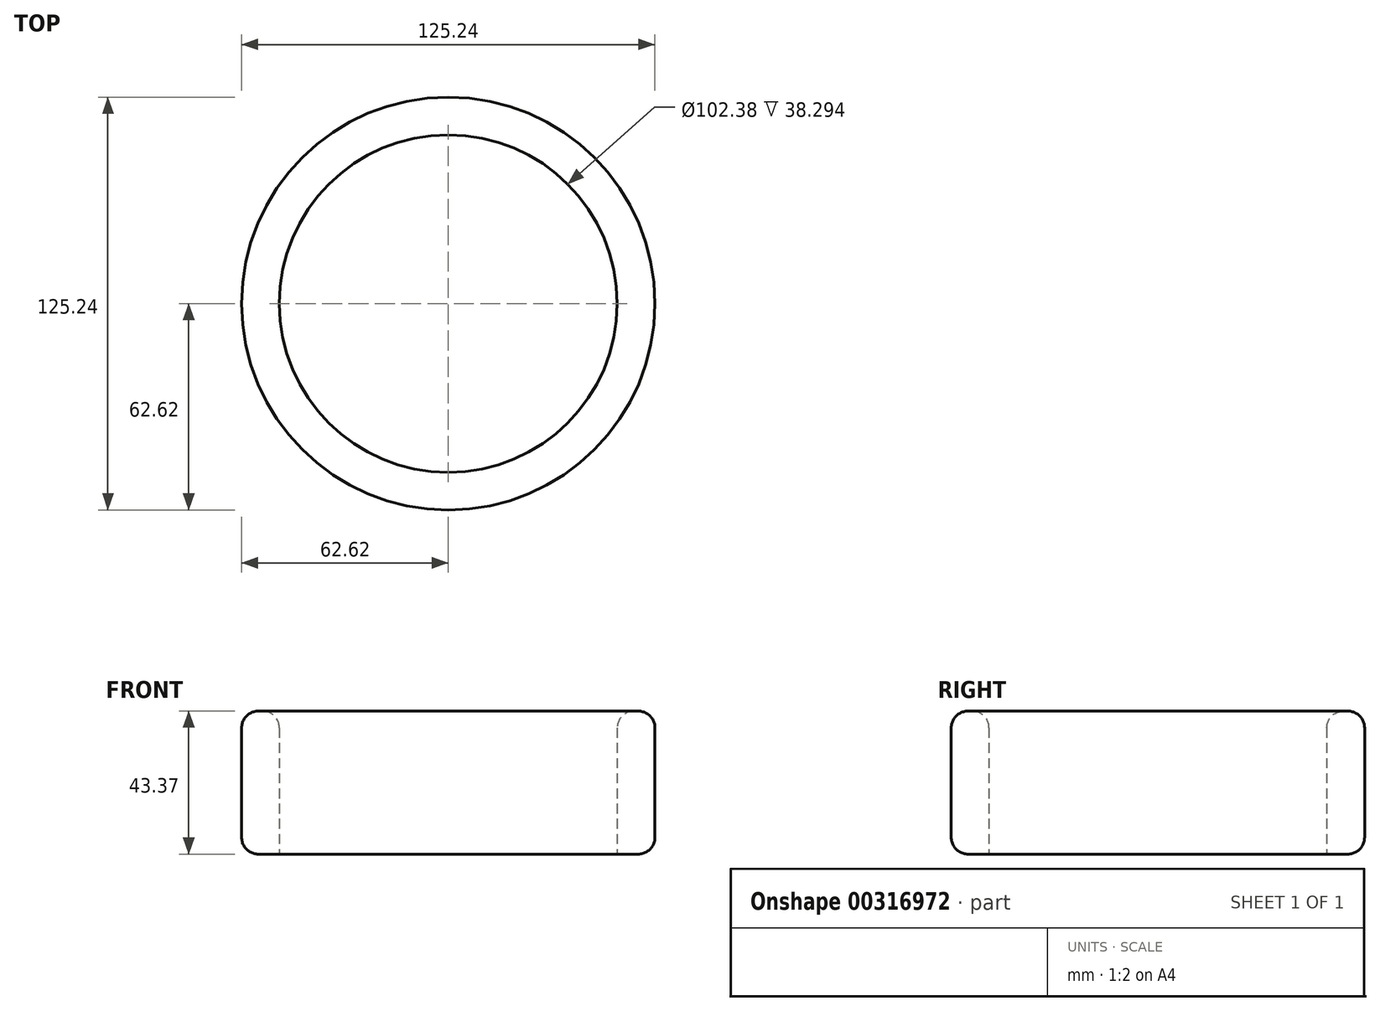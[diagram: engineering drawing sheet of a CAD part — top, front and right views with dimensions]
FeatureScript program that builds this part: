
annotation { "Feature Type Name" : "Feature", "Feature Type Description" : "" }
export const myFeature = defineFeature(function(context is Context, id is Id, definition is map)
    precondition{}
    {
        {
            var Q0;
            Q0=qCreatedBy(makeId("Top.planeOp"),FACE);
            var sketch = newSketch(context, id + "F0", { "sketchPlane" : qUnion([Q0])});
            skCircle(sketch, "E0", {"center": v(0, 0) * mm, "radius": 62.62 * mm});
            skSolve(sketch);
        }
        {
            var Q0;
            Q0 = qSketchRegion(id + "F0", true);
            extrude(context, id + "F1", {"entities" : qUnion([Q0]), "depth" : 43.37 * mm});
        }
        {
            var Q0;
            Q0=makeQuery(id+"F1.opExtrude","CAP_FACE",FACE,{"disambiguationData":[OSD([sQuery(id+"F0.wireOp",EDGE,"E0")])],"isStart":true});
            var sketch = newSketch(context, id + "F2", { "sketchPlane" : qUnion([Q0])});
            skCircle(sketch, "E1", {"center": v(0, 0) * mm, "radius": 53.37 * mm});
            skSolve(sketch);
        }
        {
            var Q0;
            Q0=makeQuery(id+"F2.imprint","IMPRINT",FACE,{"disambiguationData":[TD([[makeQuery(id+"F2.imprint","IMPRINT",EDGE,{"derivedFrom":sQuery(id+"F2.wireOp",EDGE,"E1")}),1.0]])]});
            extrude(context, id + "F3", {"entities" : qUnion([Q0]), "operationType" : NewBodyOperationType.ADD, "oppositeDirection" : true, "depth" : 5.65 * mm});
        }
        {
            var Q0;
            Q0=makeQuery(id+"F1.opExtrude","CAP_FACE",FACE,{"disambiguationData":[OSD([sQuery(id+"F0.wireOp",EDGE,"E0")])],"isStart":true});
            var sketch = newSketch(context, id + "F4", { "sketchPlane" : qUnion([Q0])});
            skCircle(sketch, "E2", {"center": v(0, 0) * mm, "radius": 51.19 * mm});
            skSolve(sketch);
        }
        {
            var Q0;
            Q0=makeQuery(id+"F4.imprint","IMPRINT",FACE,{"disambiguationData":[TD([[makeQuery(id+"F4.imprint","IMPRINT",EDGE,{"derivedFrom":sQuery(id+"F4.wireOp",EDGE,"E2")}),1.0]])]});
            extrude(context, id + "F5", {"entities" : qUnion([Q0]), "operationType" : NewBodyOperationType.REMOVE, "oppositeDirection" : true, "depth" : 64.74 * mm});
        }
        {
            var Q0;
            Q0=makeQuery(id+"F1.opExtrude","CAP_EDGE",EDGE,{"disambiguationData":[OSD([sQuery(id+"F0.wireOp",EDGE,"E0")])],"isStart":false});
            fillet(context, id + "F6", {"entities" : qUnion([Q0]), "radius" : 5.08 * mm, "tangentPropagation" : true, "allowEdgeOverflow" : false});
        }
        {
            var Q0;
            Q0=makeQuery(id+"F5.boolean.opBoolean","COPY",EDGE,{"derivedFrom":makeQuery(id+"F5.opExtrude","CAP_EDGE",EDGE,{"disambiguationData":[OSD([sQuery(id+"F4.wireOp",EDGE,"E2")])],"isStart":true})});
            var Q1;
            Q1=makeQuery(id+"F5.boolean.opBoolean","INTERSECT",EDGE,{"derivedFrom":[makeQuery(id+"F1.opExtrude","CAP_FACE",FACE,{"disambiguationData":[OSD([sQuery(id+"F0.wireOp",EDGE,"E0")])],"isStart":false}),makeQuery(id+"F5.opExtrude","SWEPT_FACE",FACE,{"disambiguationData":[OSD([sQuery(id+"F4.wireOp",EDGE,"E2")])]})]});
            fillet(context, id + "F7", {"entities" : qUnion([Q0, Q1]), "radius" : 5.08 * mm, "tangentPropagation" : true, "allowEdgeOverflow" : false});
        }
        {
            var Q0;
            Q0=makeQuery(id+"F1.opExtrude","CAP_EDGE",EDGE,{"disambiguationData":[OSD([sQuery(id+"F0.wireOp",EDGE,"E0")])],"isStart":true});
            fillet(context, id + "F8", {"entities" : qUnion([Q0]), "radius" : 5.08 * mm, "tangentPropagation" : true, "allowEdgeOverflow" : false});
        }
    });
